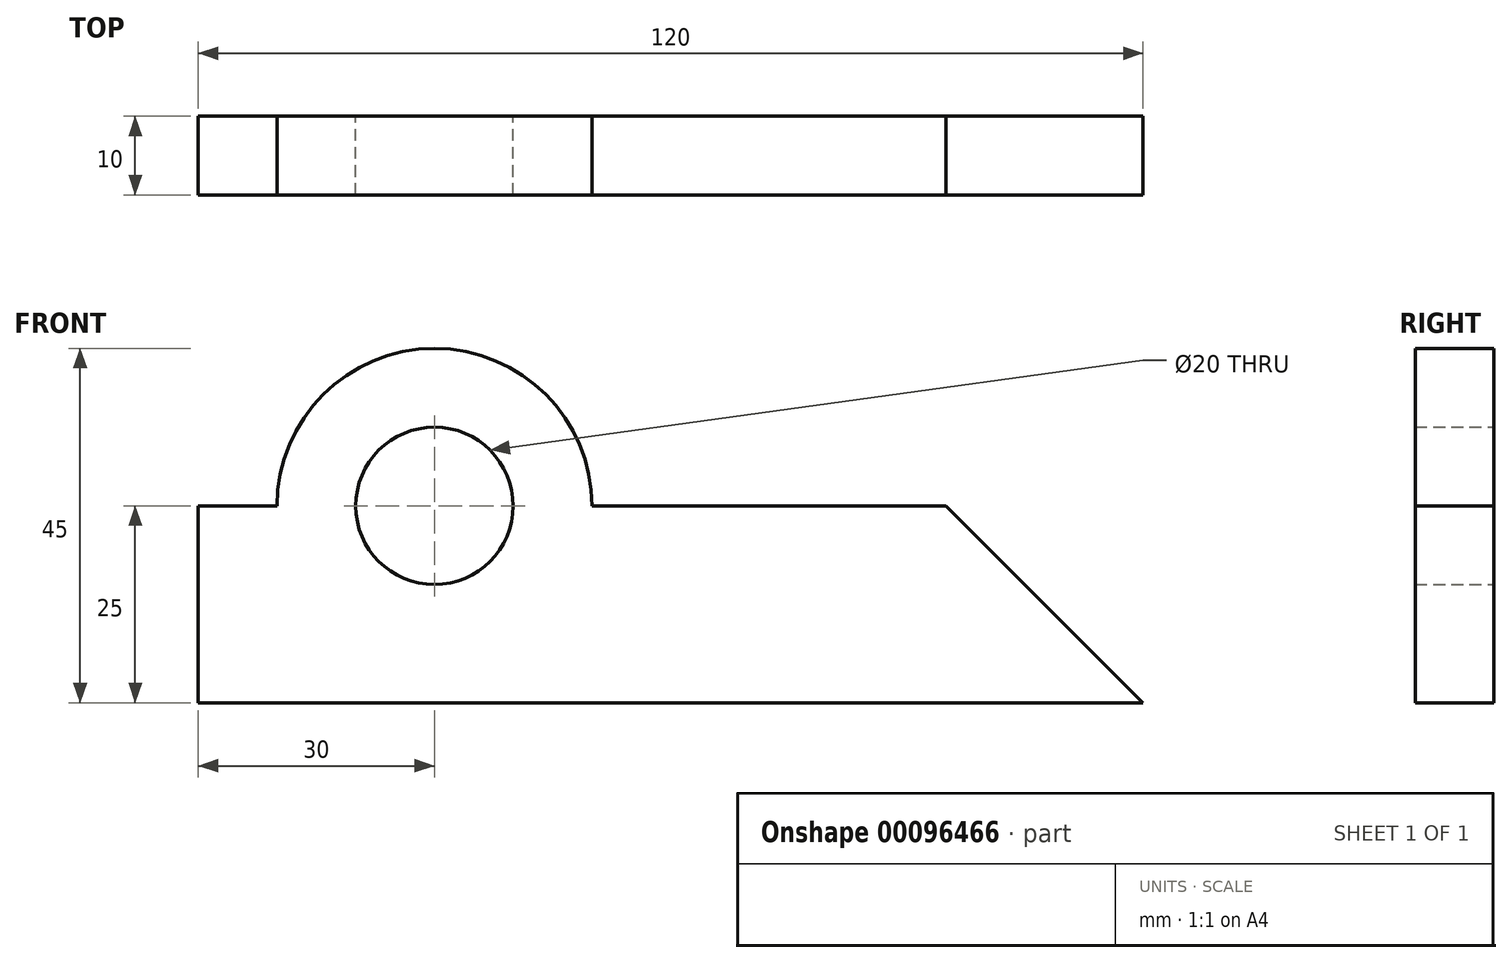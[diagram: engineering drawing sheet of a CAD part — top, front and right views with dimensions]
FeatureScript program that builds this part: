
annotation { "Feature Type Name" : "Feature", "Feature Type Description" : "" }
export const myFeature = defineFeature(function(context is Context, id is Id, definition is map)
    precondition{}
    {
        {
            var Q0;
            Q0=qCreatedBy(makeId("Front.planeOp"),FACE);
            var sketch = newSketch(context, id + "F0", { "sketchPlane" : qUnion([Q0])});
            skLineSegment(sketch, "E0", {"start": v(0, 0) * mm, "end": v(120, 0) * mm});
            skLineSegment(sketch, "E1", {"start": v(0, 0) * mm, "end": v(0, 25) * mm});
            skLineSegment(sketch, "E2", {"start": v(0, 25) * mm, "end": v(10, 25) * mm});
            skLineSegment(sketch, "E3", {"start": v(120, 0) * mm, "end": v(95, 25) * mm});
            skLineSegment(sketch, "E4", {"start": v(95, 25) * mm, "end": v(50, 25) * mm});
            skCircle(sketch, "E5", {"center": v(30, 25) * mm, "radius": 10 * mm});
            skArc(sketch, "E6", {"start": v(50, 25) * mm, "mid": v(30, 45) * mm, "end": v(10, 25) * mm});
            skLineSegment(sketch, "E7", {"start": v(10, 25) * mm, "end": v(50, 25) * mm, "construction": true});
            skSolve(sketch);
        }
        {
            var Q0;
            Q0 = qSketchRegion(id + "F0", true);
            extrude(context, id + "F1", {"entities" : qUnion([Q0]), "depth" : 10 * mm});
        }
    });
